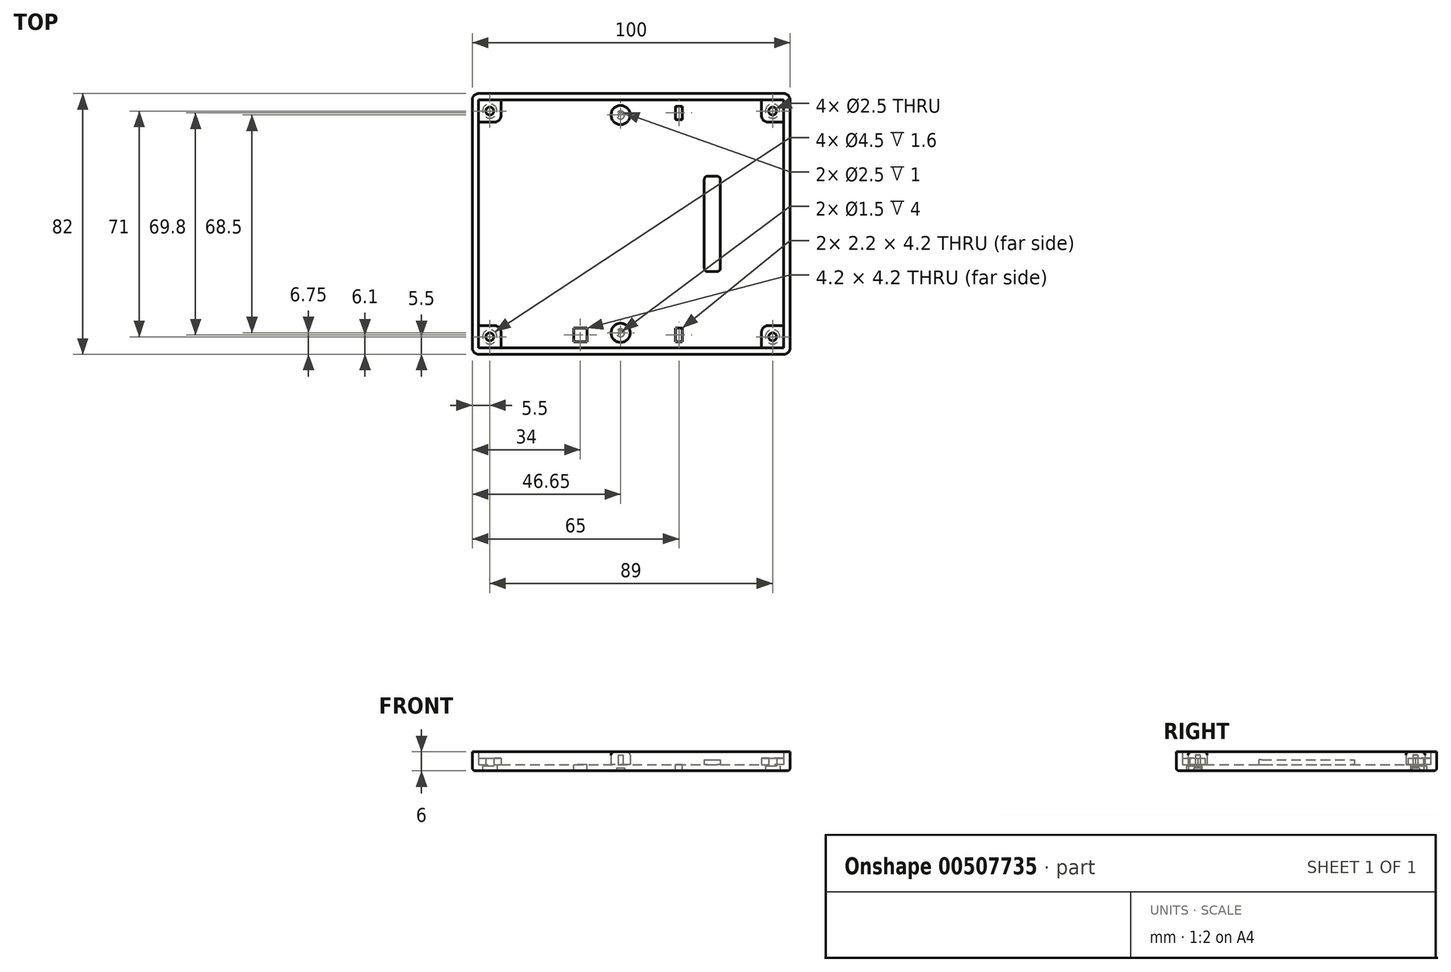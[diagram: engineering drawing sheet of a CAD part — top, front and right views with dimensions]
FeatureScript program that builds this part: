
annotation { "Feature Type Name" : "Feature", "Feature Type Description" : "" }
export const myFeature = defineFeature(function(context is Context, id is Id, definition is map)
    precondition{}
    {
        {
            var Q0;
            Q0=qCreatedBy(makeId("Top.planeOp"),FACE);
            var sketch = newSketch(context, id + "F0", { "sketchPlane" : qUnion([Q0])});
            skLineSegment(sketch, "E0.bottom", {"start": v(2, 0) * mm, "end": v(98, 0) * mm});
            skLineSegment(sketch, "E0.top", {"start": v(2, 82) * mm, "end": v(98, 82) * mm});
            skLineSegment(sketch, "E0.left", {"start": v(0, 2) * mm, "end": v(0, 80) * mm});
            skLineSegment(sketch, "E0.right", {"start": v(100, 2) * mm, "end": v(100, 80) * mm});
            skPoint(sketch, "E1.visualSharp", {"position": v(0, 82) * mm});
            skArc(sketch, "E1.filletArc", {"start": v(2, 82) * mm, "mid": v(0.59, 81.41) * mm, "end": v(0, 80) * mm});
            skPoint(sketch, "E2.visualSharp", {"position": v(0, 0) * mm});
            skArc(sketch, "E2.filletArc", {"start": v(0, 2) * mm, "mid": v(0.59, 0.59) * mm, "end": v(2, 0) * mm});
            skPoint(sketch, "E3.visualSharp", {"position": v(100, 0) * mm});
            skArc(sketch, "E3.filletArc", {"start": v(98, 0) * mm, "mid": v(99.41, 0.59) * mm, "end": v(100, 2) * mm});
            skPoint(sketch, "E4.visualSharp", {"position": v(100, 82) * mm});
            skArc(sketch, "E4.filletArc", {"start": v(100, 80) * mm, "mid": v(99.41, 81.41) * mm, "end": v(98, 82) * mm});
            skSolve(sketch);
        }
        {
            var Q0;
            Q0=makeQuery(id+"F0.imprint","IMPRINT",FACE,{"disambiguationData":[TD([[makeQuery(id+"F0.imprint","IMPRINT",EDGE,{"derivedFrom":sQuery(id+"F0.wireOp",EDGE,"E0.bottom")}),1.0]])]});
            extrude(context, id + "F1", {"entities" : qUnion([Q0]), "depth" : 2 * mm, "offsetDistance" : 25 * mm});
        }
        {
            var Q0;
            Q0=makeQuery(id+"F1.opExtrude","CAP_FACE",FACE,{"disambiguationData":[OSD([sQuery(id+"F0.wireOp",EDGE,"E0.bottom"),sQuery(id+"F0.wireOp",EDGE,"E0.top"),sQuery(id+"F0.wireOp",EDGE,"E0.left"),sQuery(id+"F0.wireOp",EDGE,"E0.right"),sQuery(id+"F0.wireOp",EDGE,"E1.filletArc"),sQuery(id+"F0.wireOp",EDGE,"E2.filletArc"),sQuery(id+"F0.wireOp",EDGE,"E3.filletArc"),sQuery(id+"F0.wireOp",EDGE,"E4.filletArc")])],"isStart":false});
            var sketch = newSketch(context, id + "F2", { "sketchPlane" : qUnion([Q0])});
            skLineSegment(sketch, "E5.0", {"start": v(2, 80) * mm, "end": v(98, 80) * mm});
            skLineSegment(sketch, "E5.1", {"start": v(98, 80) * mm, "end": v(98, 80) * mm});
            skLineSegment(sketch, "E5.2", {"start": v(2, 80) * mm, "end": v(2, 80) * mm});
            skLineSegment(sketch, "E5.3", {"start": v(98, 2) * mm, "end": v(98, 80) * mm});
            skLineSegment(sketch, "E5.4", {"start": v(2, 2) * mm, "end": v(2, 80) * mm});
            skLineSegment(sketch, "E5.5", {"start": v(2, 2) * mm, "end": v(2, 2) * mm});
            skLineSegment(sketch, "E5.6", {"start": v(2, 2) * mm, "end": v(98, 2) * mm});
            skLineSegment(sketch, "E5.7", {"start": v(98, 2) * mm, "end": v(98, 2) * mm});
            skSolve(sketch);
        }
        {
            var Q0;
            Q0=makeQuery(id+"F2.imprint","IMPRINT",FACE,{"disambiguationData":[TD([[makeQuery(id+"F2.imprint","IMPRINT",EDGE,{"derivedFrom":sQuery(id+"F2.wireOp",EDGE,"E5.0")}),1.0]])]});
            extrude(context, id + "F3", {"entities" : qUnion([Q0]), "operationType" : NewBodyOperationType.ADD, "depth" : 4 * mm, "offsetDistance" : 25 * mm});
        }
        {
            var Q0;
            Q0=makeQuery(id+"F1.opExtrude","CAP_FACE",FACE,{"disambiguationData":[OSD([sQuery(id+"F0.wireOp",EDGE,"E0.bottom"),sQuery(id+"F0.wireOp",EDGE,"E0.top"),sQuery(id+"F0.wireOp",EDGE,"E0.left"),sQuery(id+"F0.wireOp",EDGE,"E0.right"),sQuery(id+"F0.wireOp",EDGE,"E1.filletArc"),sQuery(id+"F0.wireOp",EDGE,"E2.filletArc"),sQuery(id+"F0.wireOp",EDGE,"E3.filletArc"),sQuery(id+"F0.wireOp",EDGE,"E4.filletArc")])],"isStart":false});
            var sketch = newSketch(context, id + "F4", { "sketchPlane" : qUnion([Q0])});
            skLineSegment(sketch, "E6.bottom", {"start": v(2, 2) * mm, "end": v(9, 2) * mm});
            skLineSegment(sketch, "E6.top", {"start": v(2, 9) * mm, "end": v(7, 9) * mm});
            skLineSegment(sketch, "E6.left", {"start": v(2, 2) * mm, "end": v(2, 9) * mm});
            skLineSegment(sketch, "E6.right", {"start": v(9, 2) * mm, "end": v(9, 7) * mm});
            skLineSegment(sketch, "E7.bottom", {"start": v(2, 80) * mm, "end": v(9, 80) * mm});
            skLineSegment(sketch, "E7.top", {"start": v(2, 73) * mm, "end": v(7, 73) * mm});
            skLineSegment(sketch, "E7.left", {"start": v(2, 80) * mm, "end": v(2, 73) * mm});
            skLineSegment(sketch, "E7.right", {"start": v(9, 80) * mm, "end": v(9, 75) * mm});
            skLineSegment(sketch, "E8.bottom", {"start": v(98, 2) * mm, "end": v(91, 2) * mm});
            skLineSegment(sketch, "E8.top", {"start": v(98, 9) * mm, "end": v(93, 9) * mm});
            skLineSegment(sketch, "E8.left", {"start": v(98, 2) * mm, "end": v(98, 9) * mm});
            skLineSegment(sketch, "E8.right", {"start": v(91, 2) * mm, "end": v(91, 7) * mm});
            skLineSegment(sketch, "E9.bottom", {"start": v(98, 80) * mm, "end": v(91, 80) * mm});
            skLineSegment(sketch, "E9.top", {"start": v(98, 73) * mm, "end": v(93, 73) * mm});
            skLineSegment(sketch, "E9.left", {"start": v(98, 80) * mm, "end": v(98, 73) * mm});
            skLineSegment(sketch, "E9.right", {"start": v(91, 80) * mm, "end": v(91, 75) * mm});
            skPoint(sketch, "E10.visualSharp", {"position": v(9, 9) * mm});
            skArc(sketch, "E10.filletArc", {"start": v(9, 7) * mm, "mid": v(8.41, 8.41) * mm, "end": v(7, 9) * mm});
            skPoint(sketch, "E11.visualSharp", {"position": v(9, 73) * mm});
            skArc(sketch, "E11.filletArc", {"start": v(7, 73) * mm, "mid": v(8.41, 73.59) * mm, "end": v(9, 75) * mm});
            skPoint(sketch, "E12.visualSharp", {"position": v(91, 73) * mm});
            skArc(sketch, "E12.filletArc", {"start": v(91, 75) * mm, "mid": v(91.59, 73.59) * mm, "end": v(93, 73) * mm});
            skPoint(sketch, "E13.visualSharp", {"position": v(91, 9) * mm});
            skArc(sketch, "E13.filletArc", {"start": v(93, 9) * mm, "mid": v(91.59, 8.41) * mm, "end": v(91, 7) * mm});
            skSolve(sketch);
        }
        {
            var Q0;
            Q0 = qSketchRegion(id + "F4", true);
            extrude(context, id + "F5", {"entities" : qUnion([Q0]), "operationType" : NewBodyOperationType.ADD, "depth" : 2 * mm, "offsetDistance" : 25 * mm});
        }
        {
            var Q0;
            Q0=makeQuery(id+"F1.opExtrude","CAP_FACE",FACE,{"disambiguationData":[OSD([sQuery(id+"F0.wireOp",EDGE,"E0.bottom"),sQuery(id+"F0.wireOp",EDGE,"E0.top"),sQuery(id+"F0.wireOp",EDGE,"E0.left"),sQuery(id+"F0.wireOp",EDGE,"E0.right"),sQuery(id+"F0.wireOp",EDGE,"E1.filletArc"),sQuery(id+"F0.wireOp",EDGE,"E2.filletArc"),sQuery(id+"F0.wireOp",EDGE,"E3.filletArc"),sQuery(id+"F0.wireOp",EDGE,"E4.filletArc")])],"isStart":true});
            var sketch = newSketch(context, id + "F6", { "sketchPlane" : qUnion([Q0])});
            skCircle(sketch, "E14", {"center": v(94.5, -5.5) * mm, "radius": 1.25 * mm});
            skCircle(sketch, "E15", {"center": v(94.5, -76.5) * mm, "radius": 1.25 * mm});
            skCircle(sketch, "E16", {"center": v(5.5, -76.5) * mm, "radius": 1.25 * mm});
            skCircle(sketch, "E17", {"center": v(5.5, -5.5) * mm, "radius": 1.25 * mm});
            skSolve(sketch);
        }
        {
            var Q0;
            Q0 = qSketchRegion(id + "F6", true);
            extrude(context, id + "F7", {"entities" : qUnion([Q0]), "operationType" : NewBodyOperationType.REMOVE, "oppositeDirection" : true, "depth" : 6 * mm, "offsetDistance" : 25 * mm});
        }
        {
            var Q0;
            Q0=makeQuery(id+"F1.opExtrude","CAP_FACE",FACE,{"disambiguationData":[OSD([sQuery(id+"F0.wireOp",EDGE,"E0.bottom"),sQuery(id+"F0.wireOp",EDGE,"E0.top"),sQuery(id+"F0.wireOp",EDGE,"E0.left"),sQuery(id+"F0.wireOp",EDGE,"E0.right"),sQuery(id+"F0.wireOp",EDGE,"E1.filletArc"),sQuery(id+"F0.wireOp",EDGE,"E2.filletArc"),sQuery(id+"F0.wireOp",EDGE,"E3.filletArc"),sQuery(id+"F0.wireOp",EDGE,"E4.filletArc")])],"isStart":true});
            var sketch = newSketch(context, id + "F8", { "sketchPlane" : qUnion([Q0])});
            skCircle(sketch, "E18", {"center": v(5.5, -76.5) * mm, "radius": 2.25 * mm});
            skCircle(sketch, "E19", {"center": v(5.5, -5.5) * mm, "radius": 2.25 * mm});
            skCircle(sketch, "E20", {"center": v(94.5, -5.5) * mm, "radius": 2.25 * mm});
            skCircle(sketch, "E21", {"center": v(94.5, -76.5) * mm, "radius": 2.25 * mm});
            skSolve(sketch);
        }
        {
            var Q0;
            Q0 = qSketchRegion(id + "F8", true);
            extrude(context, id + "F9", {"entities" : qUnion([Q0]), "operationType" : NewBodyOperationType.REMOVE, "oppositeDirection" : true, "depth" : 1.6 * mm, "offsetDistance" : 25 * mm});
        }
        {
            var Q0;
            Q0=makeQuery(id+"F1.opExtrude","CAP_FACE",FACE,{"disambiguationData":[OSD([sQuery(id+"F0.wireOp",EDGE,"E0.bottom"),sQuery(id+"F0.wireOp",EDGE,"E0.top"),sQuery(id+"F0.wireOp",EDGE,"E0.left"),sQuery(id+"F0.wireOp",EDGE,"E0.right"),sQuery(id+"F0.wireOp",EDGE,"E1.filletArc"),sQuery(id+"F0.wireOp",EDGE,"E2.filletArc"),sQuery(id+"F0.wireOp",EDGE,"E3.filletArc"),sQuery(id+"F0.wireOp",EDGE,"E4.filletArc")])],"isStart":false});
            var sketch = newSketch(context, id + "F10", { "sketchPlane" : qUnion([Q0])});
            skLineSegment(sketch, "E22.bottom", {"start": v(74, 26) * mm, "end": v(77, 26) * mm});
            skLineSegment(sketch, "E22.top", {"start": v(74, 56) * mm, "end": v(77, 56) * mm});
            skLineSegment(sketch, "E22.left", {"start": v(73, 27) * mm, "end": v(73, 55) * mm});
            skLineSegment(sketch, "E22.right", {"start": v(78, 27) * mm, "end": v(78, 55) * mm});
            skPoint(sketch, "E23.visualSharp", {"position": v(78, 26) * mm});
            skArc(sketch, "E23.filletArc", {"start": v(77, 26) * mm, "mid": v(77.7, 26.3) * mm, "end": v(78, 27) * mm});
            skPoint(sketch, "E24.visualSharp", {"position": v(73, 26) * mm});
            skArc(sketch, "E24.filletArc", {"start": v(73, 27) * mm, "mid": v(73.3, 26.3) * mm, "end": v(74, 26) * mm});
            skPoint(sketch, "E25.visualSharp", {"position": v(73, 56) * mm});
            skArc(sketch, "E25.filletArc", {"start": v(74, 56) * mm, "mid": v(73.3, 55.7) * mm, "end": v(73, 55) * mm});
            skPoint(sketch, "E26.visualSharp", {"position": v(78, 56) * mm});
            skArc(sketch, "E26.filletArc", {"start": v(78, 55) * mm, "mid": v(77.7, 55.7) * mm, "end": v(77, 56) * mm});
            skSolve(sketch);
        }
        {
            var Q0;
            Q0=makeQuery(id+"F1.opExtrude","CAP_EDGE",EDGE,{"disambiguationData":[OSD([sQuery(id+"F0.wireOp",EDGE,"E0.top")])],"isStart":true});
            fillet(context, id + "F11", {"entities" : qUnion([Q0]), "radius" : 1 * mm, "tangentPropagation" : true, "allowEdgeOverflow" : false});
        }
        {
            var Q0;
            Q0=makeQuery(id+"F10.imprint","IMPRINT",FACE,{"disambiguationData":[TD([[makeQuery(id+"F10.imprint","IMPRINT",EDGE,{"derivedFrom":sQuery(id+"F10.wireOp",EDGE,"E22.bottom")}),1.0]])]});
            extrude(context, id + "F12", {"entities" : qUnion([Q0]), "operationType" : NewBodyOperationType.ADD, "depth" : 1.5 * mm, "offsetDistance" : 25 * mm});
        }
        {
            var Q0;
            Q0=makeQuery(id+"F1.opExtrude","CAP_FACE",FACE,{"disambiguationData":[OSD([sQuery(id+"F0.wireOp",EDGE,"E0.bottom"),sQuery(id+"F0.wireOp",EDGE,"E0.top"),sQuery(id+"F0.wireOp",EDGE,"E0.left"),sQuery(id+"F0.wireOp",EDGE,"E0.right"),sQuery(id+"F0.wireOp",EDGE,"E1.filletArc"),sQuery(id+"F0.wireOp",EDGE,"E2.filletArc"),sQuery(id+"F0.wireOp",EDGE,"E3.filletArc"),sQuery(id+"F0.wireOp",EDGE,"E4.filletArc")])],"isStart":false});
            var sketch = newSketch(context, id + "F13", { "sketchPlane" : qUnion([Q0])});
            skLineSegment(sketch, "E27.bottom", {"start": v(66.1, 78) * mm, "end": v(63.9, 78) * mm});
            skLineSegment(sketch, "E27.top", {"start": v(66.1, 73.8) * mm, "end": v(63.9, 73.8) * mm});
            skLineSegment(sketch, "E27.left", {"start": v(66.1, 78) * mm, "end": v(66.1, 73.8) * mm});
            skLineSegment(sketch, "E27.right", {"start": v(63.9, 78) * mm, "end": v(63.9, 73.8) * mm});
            skLineSegment(sketch, "E28.bottom", {"start": v(36.1, 78) * mm, "end": v(31.9, 78) * mm});
            skLineSegment(sketch, "E28.top", {"start": v(36.1, 73.8) * mm, "end": v(31.9, 73.8) * mm});
            skLineSegment(sketch, "E28.left", {"start": v(36.1, 78) * mm, "end": v(36.1, 73.8) * mm});
            skLineSegment(sketch, "E28.right", {"start": v(31.9, 78) * mm, "end": v(31.9, 73.8) * mm});
            skLineSegment(sketch, "E29.bottom", {"start": v(66.1, 4) * mm, "end": v(63.9, 4) * mm});
            skLineSegment(sketch, "E29.top", {"start": v(66.1, 8.2) * mm, "end": v(63.9, 8.2) * mm});
            skLineSegment(sketch, "E29.left", {"start": v(66.1, 4) * mm, "end": v(66.1, 8.2) * mm});
            skLineSegment(sketch, "E29.right", {"start": v(63.9, 4) * mm, "end": v(63.9, 8.2) * mm});
            skLineSegment(sketch, "E30.bottom", {"start": v(36.1, 8.2) * mm, "end": v(31.9, 8.2) * mm});
            skLineSegment(sketch, "E30.top", {"start": v(36.1, 4) * mm, "end": v(31.9, 4) * mm});
            skLineSegment(sketch, "E30.left", {"start": v(36.1, 8.2) * mm, "end": v(36.1, 4) * mm});
            skLineSegment(sketch, "E30.right", {"start": v(31.9, 8.2) * mm, "end": v(31.9, 4) * mm});
            skCircle(sketch, "E31", {"center": v(46.65, 75.25) * mm, "radius": 1.25 * mm});
            skCircle(sketch, "E32", {"center": v(46.65, 6.75) * mm, "radius": 1.25 * mm});
            skSolve(sketch);
        }
        {
            var Q0;
            Q0=makeQuery(id+"F1.opExtrude","CAP_FACE",FACE,{"disambiguationData":[OSD([sQuery(id+"F0.wireOp",EDGE,"E0.bottom"),sQuery(id+"F0.wireOp",EDGE,"E0.top"),sQuery(id+"F0.wireOp",EDGE,"E0.left"),sQuery(id+"F0.wireOp",EDGE,"E0.right"),sQuery(id+"F0.wireOp",EDGE,"E1.filletArc"),sQuery(id+"F0.wireOp",EDGE,"E2.filletArc"),sQuery(id+"F0.wireOp",EDGE,"E3.filletArc"),sQuery(id+"F0.wireOp",EDGE,"E4.filletArc")])],"isStart":false});
            var sketch = newSketch(context, id + "F14", { "sketchPlane" : qUnion([Q0])});
            skCircle(sketch, "E33", {"center": v(46.65, 75.25) * mm, "radius": 3 * mm});
            skCircle(sketch, "E34", {"center": v(46.65, 6.75) * mm, "radius": 3 * mm});
            skSolve(sketch);
        }
        {
            var Q0;
            Q0 = qSketchRegion(id + "F14", true);
            extrude(context, id + "F15", {"entities" : qUnion([Q0]), "operationType" : NewBodyOperationType.ADD, "depth" : 4 * mm, "offsetDistance" : 25 * mm});
        }
        {
            var Q0;
            Q0=makeQuery(id+"F15.opExtrude","CAP_EDGE",EDGE,{"disambiguationData":[OSD([sQuery(id+"F14.wireOp",EDGE,"E33")])],"isStart":false});
            var Q1;
            Q1=makeQuery(id+"F15.opExtrude","CAP_EDGE",EDGE,{"disambiguationData":[OSD([sQuery(id+"F14.wireOp",EDGE,"E34")])],"isStart":false});
            fillet(context, id + "F16", {"entities" : qUnion([Q0, Q1]), "radius" : 1 * mm, "tangentPropagation" : true, "allowEdgeOverflow" : false});
        }
        {
            var Q0;
            Q0=makeQuery(id+"F1.opExtrude","CAP_FACE",FACE,{"disambiguationData":[OSD([sQuery(id+"F0.wireOp",EDGE,"E0.bottom"),sQuery(id+"F0.wireOp",EDGE,"E0.top"),sQuery(id+"F0.wireOp",EDGE,"E0.left"),sQuery(id+"F0.wireOp",EDGE,"E0.right"),sQuery(id+"F0.wireOp",EDGE,"E1.filletArc"),sQuery(id+"F0.wireOp",EDGE,"E2.filletArc"),sQuery(id+"F0.wireOp",EDGE,"E3.filletArc"),sQuery(id+"F0.wireOp",EDGE,"E4.filletArc")])],"isStart":true});
            var sketch = newSketch(context, id + "F17", { "sketchPlane" : qUnion([Q0])});
            skCircle(sketch, "E35", {"center": v(46.65, -75.25) * mm, "radius": 1.25 * mm});
            skCircle(sketch, "E36", {"center": v(46.65, -6.75) * mm, "radius": 1.25 * mm});
            skSolve(sketch);
        }
        {
            var Q0;
            Q0 = qSketchRegion(id + "F17", true);
            extrude(context, id + "F18", {"entities" : qUnion([Q0]), "operationType" : NewBodyOperationType.REMOVE, "oppositeDirection" : true, "depth" : 1 * mm, "offsetDistance" : 25 * mm});
        }
        {
            var Q0;
            Q0=makeQuery(id+"F18.boolean.opBoolean","COPY",FACE,{"derivedFrom":makeQuery(id+"F18.opExtrude","CAP_FACE",FACE,{"disambiguationData":[OSD([sQuery(id+"F17.wireOp",EDGE,"E36")])],"isStart":false})});
            var sketch = newSketch(context, id + "F19", { "sketchPlane" : qUnion([Q0])});
            skCircle(sketch, "E37", {"center": v(46.65, -6.75) * mm, "radius": 0.75 * mm});
            skCircle(sketch, "E38", {"center": v(46.65, -75.25) * mm, "radius": 0.75 * mm});
            skSolve(sketch);
        }
        {
            var Q0;
            Q0 = qSketchRegion(id + "F19", true);
            extrude(context, id + "F20", {"entities" : qUnion([Q0]), "operationType" : NewBodyOperationType.REMOVE, "oppositeDirection" : true, "depth" : 4 * mm, "offsetDistance" : 25 * mm});
        }
        {
            var Q0;
            Q0=makeQuery(id+"F13.imprint","IMPRINT",FACE,{"disambiguationData":[TD([[makeQuery(id+"F13.imprint","IMPRINT",EDGE,{"derivedFrom":sQuery(id+"F13.wireOp",EDGE,"E28.bottom")}),1.0]])]});
            var sketch = newSketch(context, id + "F21", { "sketchPlane" : qUnion([Q0])});
            skSolve(sketch);
        }
        {
            var Q0;
            Q0=makeQuery(id+"F13.imprint","IMPRINT",FACE,{"disambiguationData":[TD([[makeQuery(id+"F13.imprint","IMPRINT",EDGE,{"derivedFrom":sQuery(id+"F13.wireOp",EDGE,"E27.bottom")}),1.0]])]});
            var Q1;
            Q1=makeQuery(id+"F13.imprint","IMPRINT",FACE,{"disambiguationData":[TD([[makeQuery(id+"F13.imprint","IMPRINT",EDGE,{"derivedFrom":sQuery(id+"F13.wireOp",EDGE,"E29.bottom")}),-1.0]])]});
            var Q2;
            Q2=makeQuery(id+"F13.imprint","IMPRINT",FACE,{"disambiguationData":[TD([[makeQuery(id+"F13.imprint","IMPRINT",EDGE,{"derivedFrom":sQuery(id+"F13.wireOp",EDGE,"E30.bottom")}),1.0]])]});
            var Q3;
            Q3=makeQuery(id+"F21.imprint","IMPRINT",FACE,{"disambiguationData":[TD([[makeQuery(id+"F21.imprint","IMPRINT",EDGE,{"derivedFrom":makeQuery(id+"F13.imprint","IMPRINT",EDGE,{"derivedFrom":sQuery(id+"F13.wireOp",EDGE,"E28.bottom")})}),1.0]])]});
            extrude(context, id + "F22", {"entities" : qUnion([Q0, Q1, Q2, Q3]), "operationType" : NewBodyOperationType.REMOVE, "oppositeDirection" : true, "depth" : 2 * mm, "offsetDistance" : 25 * mm});
        }
    });
